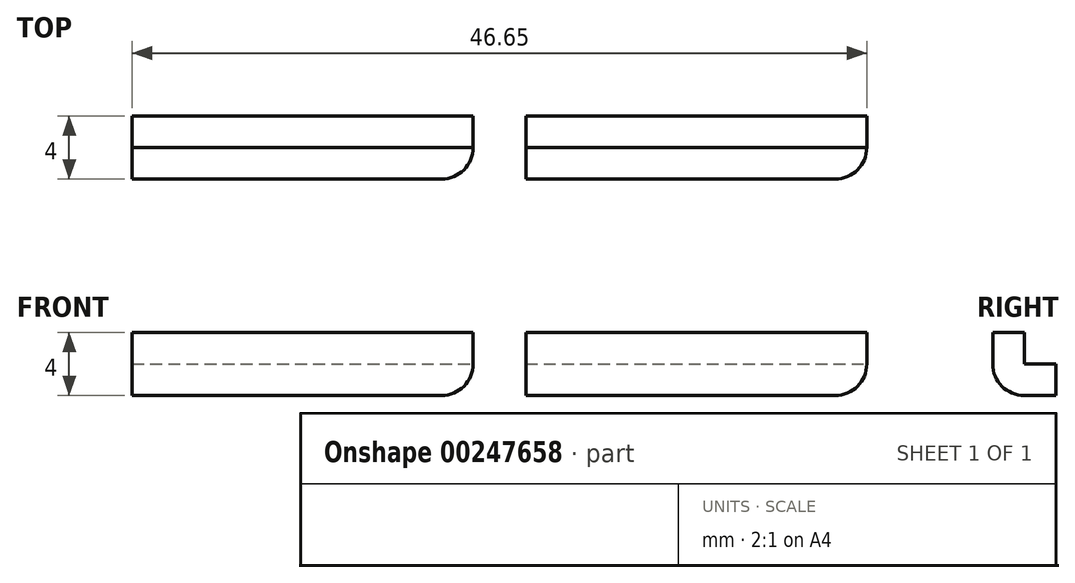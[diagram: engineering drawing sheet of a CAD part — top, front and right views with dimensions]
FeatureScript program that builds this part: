
annotation { "Feature Type Name" : "Feature", "Feature Type Description" : "" }
export const myFeature = defineFeature(function(context is Context, id is Id, definition is map)
    precondition{}
    {
        {
            var Q0;
            Q0=qCreatedBy(makeId("Front.planeOp"),FACE);
            var sketch = newSketch(context, id + "F0", { "sketchPlane" : qUnion([Q0])});
            skLineSegment(sketch, "E0", {"start": v(-75.07, 2) * mm, "end": v(-75.07, 0) * mm});
            skLineSegment(sketch, "E1", {"start": v(-75.07, 0) * mm, "end": v(-96.72, 0) * mm});
            skLineSegment(sketch, "E2", {"start": v(-96.72, 2) * mm, "end": v(-75.07, 2) * mm});
            skLineSegment(sketch, "E3", {"start": v(-96.72, 2) * mm, "end": v(-96.72, 0) * mm});
            skLineSegment(sketch, "E4.MirrorCS", {"start": v(96.72, 2) * mm, "end": v(75.07, 2) * mm});
            skLineSegment(sketch, "E5.MirrorCS", {"start": v(75.07, 0) * mm, "end": v(96.72, 0) * mm});
            skLineSegment(sketch, "E6.MirrorCS", {"start": v(96.72, 2) * mm, "end": v(96.72, 0) * mm});
            skLineSegment(sketch, "E7.MirrorCS", {"start": v(75.07, 2) * mm, "end": v(75.07, 0) * mm});
            skSolve(sketch);
        }
        {
            var Q0;
            Q0=makeQuery(id+"F0.imprint","IMPRINT",FACE,{"disambiguationData":[TD([[makeQuery(id+"F0.imprint","IMPRINT",EDGE,{"derivedFrom":sQuery(id+"F0.wireOp",EDGE,"E0")}),-1.0]])]});
            var Q1;
            Q1=makeQuery(id+"F0.imprint","IMPRINT",FACE,{"disambiguationData":[TD([[makeQuery(id+"F0.imprint","IMPRINT",EDGE,{"derivedFrom":sQuery(id+"F0.wireOp",EDGE,"E4.MirrorCS")}),1.0]])]});
            extrude(context, id + "F1", {"entities" : qUnion([Q0, Q1]), "depth" : 4 * mm});
        }
        {
            var Q0;
            Q0=makeQuery(id+"F1.opExtrude","SWEPT_FACE",FACE,{"disambiguationData":[OSD([sQuery(id+"F0.wireOp",EDGE,"E2")])]});
            var sketch = newSketch(context, id + "F2", { "sketchPlane" : qUnion([Q0])});
            skLineSegment(sketch, "E8", {"start": v(-96.72, -2) * mm, "end": v(-75.07, -2) * mm});
            skLineSegment(sketch, "E9", {"start": v(-75.07, -2) * mm, "end": v(-75.07, -4) * mm});
            skLineSegment(sketch, "E10", {"start": v(-75.07, -4) * mm, "end": v(-96.72, -4) * mm});
            skLineSegment(sketch, "E11", {"start": v(-96.72, -4) * mm, "end": v(-96.72, -2) * mm});
            skSolve(sketch);
        }
        {
            var Q0;
            Q0=makeQuery(id+"F1.opExtrude","SWEPT_FACE",FACE,{"disambiguationData":[OSD([sQuery(id+"F0.wireOp",EDGE,"E4.MirrorCS")])]});
            var sketch = newSketch(context, id + "F3", { "sketchPlane" : qUnion([Q0])});
            skLineSegment(sketch, "E12", {"start": v(75.07, -2) * mm, "end": v(96.72, -2) * mm});
            skLineSegment(sketch, "E13", {"start": v(96.72, -2) * mm, "end": v(96.72, -4) * mm});
            skLineSegment(sketch, "E14", {"start": v(96.72, -4) * mm, "end": v(75.07, -4) * mm});
            skLineSegment(sketch, "E15", {"start": v(75.07, -4) * mm, "end": v(75.07, -2) * mm});
            skSolve(sketch);
        }
        {
            var Q0;
            Q0=makeQuery(id+"F2.imprint","IMPRINT",FACE,{"disambiguationData":[TD([[makeQuery(id+"F2.imprint","IMPRINT",EDGE,{"derivedFrom":sQuery(id+"F2.wireOp",EDGE,"E8")}),-1.0]])]});
            var Q1;
            Q1=makeQuery(id+"F3.imprint","IMPRINT",FACE,{"disambiguationData":[TD([[makeQuery(id+"F3.imprint","IMPRINT",EDGE,{"derivedFrom":sQuery(id+"F3.wireOp",EDGE,"E12")}),-1.0]])]});
            extrude(context, id + "F4", {"entities" : qUnion([Q0, Q1]), "depth" : 2 * mm});
        }
        {
            var Q0;
            Q0=makeQuery(id+"F1.opExtrude","SWEPT_BODY",BODY,{"disambiguationData":[OSD([sQuery(id+"F0.wireOp",EDGE,"E0"),sQuery(id+"F0.wireOp",EDGE,"E1"),sQuery(id+"F0.wireOp",EDGE,"E2"),sQuery(id+"F0.wireOp",EDGE,"E3")])]});
            var Q1;
            Q1=makeQuery(id+"F4.opExtrude","SWEPT_BODY",BODY,{"disambiguationData":[OSD([sQuery(id+"F2.wireOp",EDGE,"E8"),sQuery(id+"F2.wireOp",EDGE,"E9"),sQuery(id+"F2.wireOp",EDGE,"E10"),sQuery(id+"F2.wireOp",EDGE,"E11")])]});
            booleanBodies(context, id + "F5", {"operationType" : BooleanOperationType.UNION, "tools" : qUnion([Q0, Q1])});
        }
        {
            var Q0;
            Q0=makeQuery(id+"F1.opExtrude","SWEPT_BODY",BODY,{"disambiguationData":[OSD([sQuery(id+"F0.wireOp",EDGE,"E4.MirrorCS"),sQuery(id+"F0.wireOp",EDGE,"E5.MirrorCS"),sQuery(id+"F0.wireOp",EDGE,"E6.MirrorCS"),sQuery(id+"F0.wireOp",EDGE,"E7.MirrorCS")])]});
            var Q1;
            Q1=makeQuery(id+"F4.opExtrude","SWEPT_BODY",BODY,{"disambiguationData":[OSD([sQuery(id+"F3.wireOp",EDGE,"E12"),sQuery(id+"F3.wireOp",EDGE,"E13"),sQuery(id+"F3.wireOp",EDGE,"E14"),sQuery(id+"F3.wireOp",EDGE,"E15")])]});
            booleanBodies(context, id + "F6", {"operationType" : BooleanOperationType.UNION, "tools" : qUnion([Q0, Q1])});
        }
        {
            var Q0;
            Q0=makeQuery(id+"F1.opExtrude","SWEPT_EDGE",EDGE,{"disambiguationData":[OSD([sQuery(id+"F0.wireOp",EDGE,"E1"),sQuery(id+"F0.wireOp",EDGE,"E3")])]});
            var Q1;
            Q1=makeQuery(id+"F5.opBoolean","MERGE",EDGE,{"derivedFrom":[makeQuery(id+"F1.opExtrude","CAP_EDGE",EDGE,{"disambiguationData":[OSD([sQuery(id+"F0.wireOp",EDGE,"E3")])],"isStart":false}),makeQuery(id+"F4.opExtrude","SWEPT_EDGE",EDGE,{"disambiguationData":[OSD([sQuery(id+"F2.wireOp",EDGE,"E10"),sQuery(id+"F2.wireOp",EDGE,"E11")])]})]});
            var Q2;
            Q2=makeQuery(id+"F1.opExtrude","CAP_EDGE",EDGE,{"disambiguationData":[OSD([sQuery(id+"F0.wireOp",EDGE,"E1")])],"isStart":false});
            var Q3;
            Q3=makeQuery(id+"F5.opBoolean","MERGE",EDGE,{"derivedFrom":[makeQuery(id+"F1.opExtrude","CAP_EDGE",EDGE,{"disambiguationData":[OSD([sQuery(id+"F0.wireOp",EDGE,"E0")])],"isStart":false}),makeQuery(id+"F4.opExtrude","SWEPT_EDGE",EDGE,{"disambiguationData":[OSD([sQuery(id+"F2.wireOp",EDGE,"E9"),sQuery(id+"F2.wireOp",EDGE,"E10")])]})]});
            var Q4;
            Q4=makeQuery(id+"F1.opExtrude","SWEPT_EDGE",EDGE,{"disambiguationData":[OSD([sQuery(id+"F0.wireOp",EDGE,"E0"),sQuery(id+"F0.wireOp",EDGE,"E1")])]});
            var Q5;
            Q5=makeQuery(id+"F1.opExtrude","SWEPT_EDGE",EDGE,{"disambiguationData":[OSD([sQuery(id+"F0.wireOp",EDGE,"E5.MirrorCS"),sQuery(id+"F0.wireOp",EDGE,"E6.MirrorCS")])]});
            var Q6;
            Q6=makeQuery(id+"F6.opBoolean","MERGE",EDGE,{"derivedFrom":[makeQuery(id+"F1.opExtrude","CAP_EDGE",EDGE,{"disambiguationData":[OSD([sQuery(id+"F0.wireOp",EDGE,"E6.MirrorCS")])],"isStart":false}),makeQuery(id+"F4.opExtrude","SWEPT_EDGE",EDGE,{"disambiguationData":[OSD([sQuery(id+"F3.wireOp",EDGE,"E13"),sQuery(id+"F3.wireOp",EDGE,"E14")])]})]});
            var Q7;
            Q7=makeQuery(id+"F1.opExtrude","CAP_EDGE",EDGE,{"disambiguationData":[OSD([sQuery(id+"F0.wireOp",EDGE,"E5.MirrorCS")])],"isStart":false});
            fillet(context, id + "F7", {"entities" : qUnion([Q0, Q1, Q2, Q3, Q4, Q5, Q6, Q7]), "radius" : 2 * mm, "tangentPropagation" : true, "allowEdgeOverflow" : false});
        }
        {
            var Q0;
            Q0=makeQuery(id+"F1.opExtrude","SWEPT_BODY",BODY,{"disambiguationData":[OSD([sQuery(id+"F0.wireOp",EDGE,"E0"),sQuery(id+"F0.wireOp",EDGE,"E1"),sQuery(id+"F0.wireOp",EDGE,"E2"),sQuery(id+"F0.wireOp",EDGE,"E3")])]});
            deleteBodies(context, id + "F8", {"entities" : qUnion([Q0])});
        }
        {
            var Q0;
            Q0=makeQuery(id+"F1.opExtrude","SWEPT_BODY",BODY,{"disambiguationData":[OSD([sQuery(id+"F0.wireOp",EDGE,"E4.MirrorCS"),sQuery(id+"F0.wireOp",EDGE,"E5.MirrorCS"),sQuery(id+"F0.wireOp",EDGE,"E6.MirrorCS"),sQuery(id+"F0.wireOp",EDGE,"E7.MirrorCS")])]});
            transform(context, id + "F9", {"entities" : qUnion([Q0]), "transformType" : TransformType.TRANSLATION_3D, "dx" : -25 * mm, "dy" : 0 * mm, "dz" : 0 * mm, "makeCopy" : true});
        }
    });
